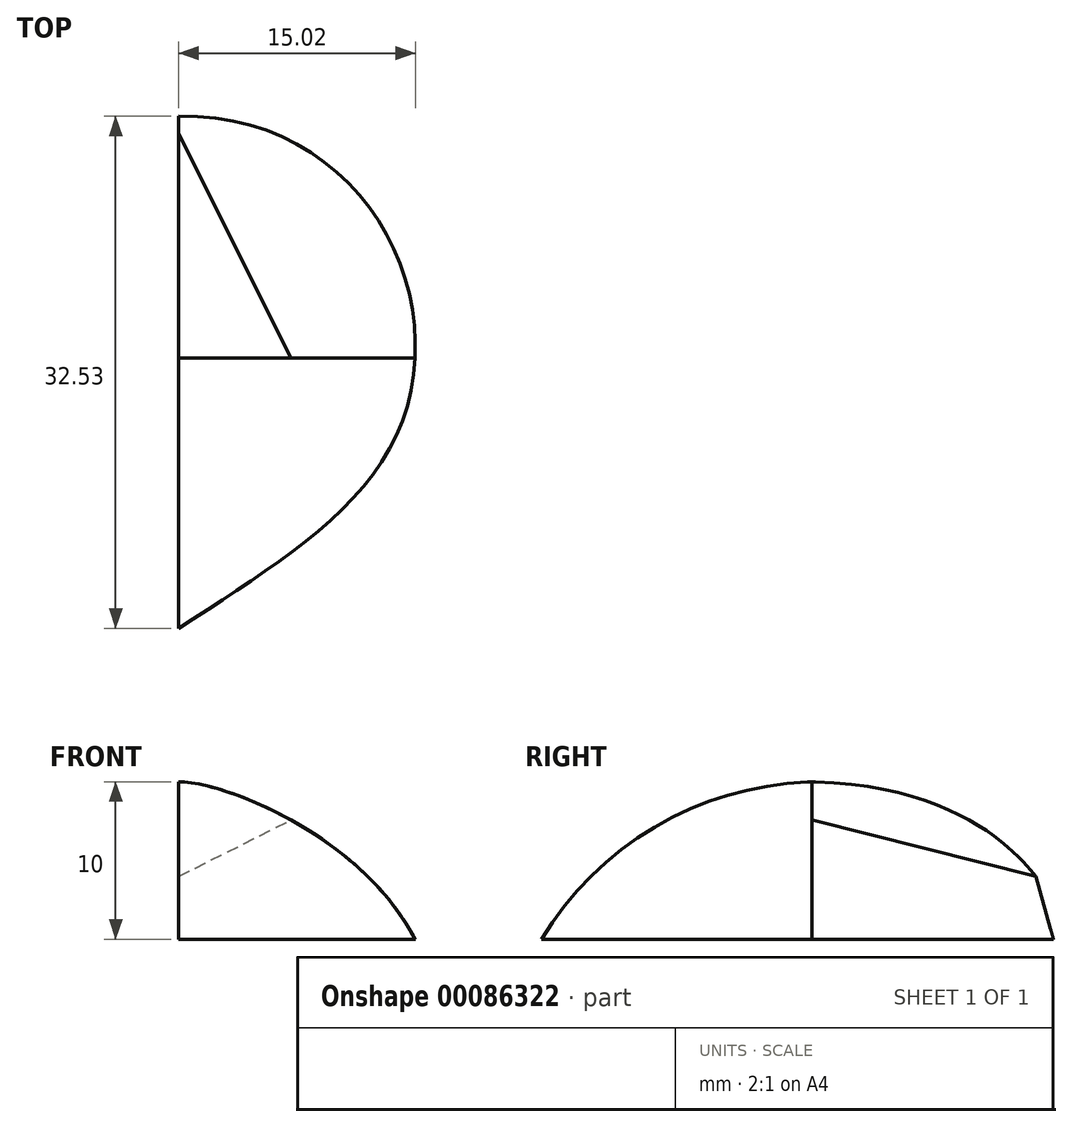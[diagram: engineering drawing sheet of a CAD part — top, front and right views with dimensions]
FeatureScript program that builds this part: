
annotation { "Feature Type Name" : "Feature", "Feature Type Description" : "" }
export const myFeature = defineFeature(function(context is Context, id is Id, definition is map)
    precondition{}
    {
        {
            var Q0;
            Q0=qCreatedBy(makeId("Front.planeOp"),FACE);
            var sketch = newSketch(context, id + "F0", { "sketchPlane" : qUnion([Q0])});
            skLineSegment(sketch, "E0", {"start": v(0, 10) * mm, "end": v(0, -10) * mm, "construction": true});
            skLineSegment(sketch, "E1", {"start": v(-15, 0) * mm, "end": v(15, 0) * mm, "construction": true});
            skFitSpline(sketch, "E2", {"points": [v(0, 10) * mm, v(15, 0) * mm], "startDerivative": vector(7.51, 0.28) * mm, "endDerivative": vector(10.5, -20.31) * mm});
            skSolve(sketch);
        }
        {
            var Q0;
            Q0=qCreatedBy(makeId("Right.planeOp"),FACE);
            var sketch = newSketch(context, id + "F1", { "sketchPlane" : qUnion([Q0])});
            skLineSegment(sketch, "E3", {"start": v(0, 0) * mm, "end": v(-19.36, 0) * mm, "construction": true});
            skLineSegment(sketch, "E4", {"start": v(-19.36, 0) * mm, "end": v(-19.36, -5) * mm, "construction": true});
            skCircle(sketch, "E5", {"center": v(0, -10) * mm, "radius": 20 * mm, "construction": true});
            skPoint(sketch, "E5.second.point", {"position": v(0, 10) * mm});
            skPoint(sketch, "E5.third.point", {"position": v(14.2, 4.08) * mm});
            skArc(sketch, "E6", {"start": v(0, 10) * mm, "mid": v(-9.86, 7.19) * mm, "end": v(-17.18, 0) * mm});
            skSolve(sketch);
        }
        {
            var Q0;
            Q0=qCreatedBy(makeId("Top.planeOp"),FACE);
            var sketch = newSketch(context, id + "F2", { "sketchPlane" : qUnion([Q0])});
            skFitSpline(sketch, "E7", {"points": [v(15, 0) * mm, v(0, -17.18) * mm], "startDerivative": vector(-1, -25.08) * mm, "endDerivative": vector(-21.12, -13.97) * mm});
            skSolve(sketch);
        }
        {
            var Q0;
            Q0=sQuery(id+"F1.wireOp",EDGE,"E6");
            var Q1;
            Q1=sQuery(id+"F0.wireOp",EDGE,"E2");
            var Q2;
            Q2=sQuery(id+"F2.wireOp",EDGE,"E7");
            loft(context, id + "F3", {"bodyType" : ToolBodyType.SURFACE, "addGuides" : true, "wireProfilesArray" : [{ "wireProfileEntities" : qUnion([Q0]) }, { "wireProfileEntities" : qUnion([Q1]) }], "guidesArray" : [{ "guideEntities" : qUnion([Q2]), "guideDerivativeType" : LoftGuideDerivativeType.DEFAULT, "guideDerivativeMagnitude" : 1 }]});
        }
        {
            var Q0;
            Q0=qCreatedBy(makeId("Right.planeOp"),FACE);
            var sketch = newSketch(context, id + "F4", { "sketchPlane" : qUnion([Q0])});
            skFitSpline(sketch, "E8", {"points": [v(0, 10) * mm, v(14.23, 4) * mm], "startDerivative": vector(28.01, -0.53) * mm, "endDerivative": vector(3.31, -4.17) * mm});
            skLineSegment(sketch, "E9", {"start": v(15.35, 0) * mm, "end": v(14.23, 4) * mm});
            skSolve(sketch);
        }
        {
            var Q0;
            Q0=qCreatedBy(makeId("Top.planeOp"),FACE);
            var sketch = newSketch(context, id + "F5", { "sketchPlane" : qUnion([Q0])});
            skFitSpline(sketch, "E10", {"points": [v(0, 15.35) * mm, v(15, 0) * mm], "startDerivative": vector(27.76, 0.7) * mm, "endDerivative": vector(-1.27, -23.7) * mm});
            skSolve(sketch);
        }
        {
            var Q0;
            Q0 = qConstructionFilter(qBodyType(qCreatedBy(id + "F4" ,EDGE), BodyType.WIRE), ConstructionObject.NO);
            var Q1;
            Q1=makeQuery(id+"F3.opLoft","MID_CAP_EDGE",EDGE,{"disambiguationData":[OSD([sQuery(id+"F0.wireOp",VERTEX,"E2.start"),sQuery(id+"F0.wireOp",EDGE,"E2"),sQuery(id+"F2.wireOp",EDGE,"E7")])],"capPos":1.0});
            var Q2;
            Q2 = qConstructionFilter(qBodyType(qCreatedBy(id + "F5" ,EDGE), BodyType.WIRE), ConstructionObject.NO);
            loft(context, id + "F6", {"bodyType" : ToolBodyType.SURFACE, "addGuides" : true, "wireProfilesArray" : [{ "wireProfileEntities" : qUnion([Q0]) }, { "wireProfileEntities" : qUnion([Q1]) }], "guidesArray" : [{ "guideEntities" : qUnion([Q2]), "guideDerivativeType" : LoftGuideDerivativeType.DEFAULT, "guideDerivativeMagnitude" : 1 }]});
        }
    });
